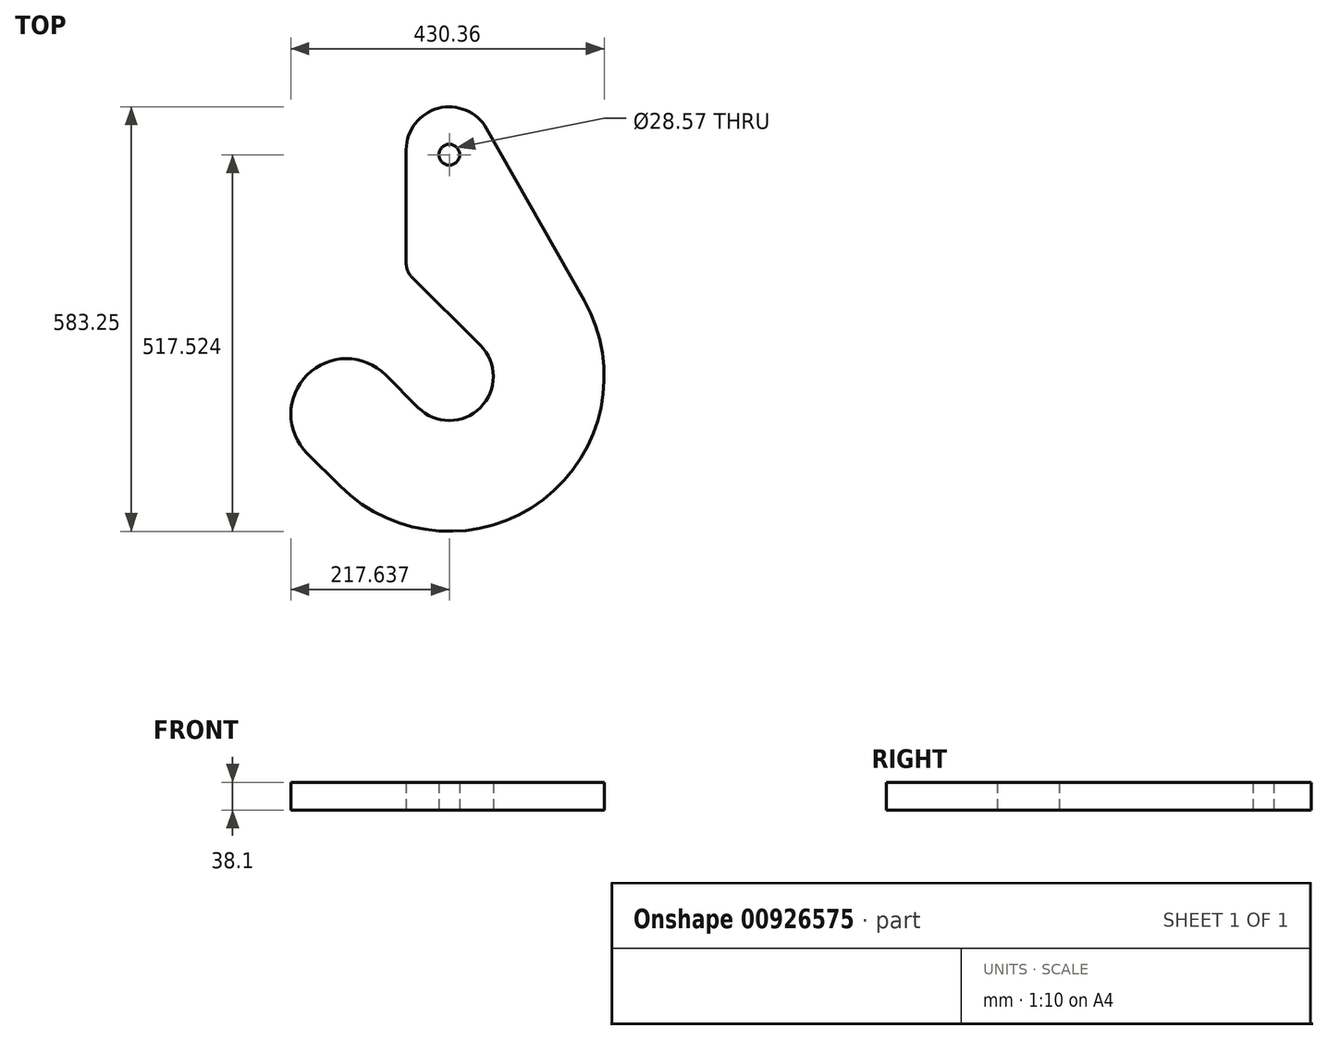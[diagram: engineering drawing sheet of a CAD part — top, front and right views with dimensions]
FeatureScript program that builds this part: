
annotation { "Feature Type Name" : "Feature", "Feature Type Description" : "" }
export const myFeature = defineFeature(function(context is Context, id is Id, definition is map)
    precondition{}
    {
        {
            var Q0;
            Q0=qCreatedBy(makeId("Top.planeOp"),FACE);
            var sketch = newSketch(context, id + "F0", { "sketchPlane" : qUnion([Q0])});
            skCircle(sketch, "E0", {"center": v(-102.2, 33.62) * mm, "radius": 60.33 * mm, "construction": true});
            skLineSegment(sketch, "E1", {"start": v(-102.2, 33.62) * mm, "end": v(-59.55, 76.28) * mm, "construction": true});
            skLineSegment(sketch, "E2", {"start": v(-102.2, 33.62) * mm, "end": v(-144.86, -9.03) * mm, "construction": true});
            skLineSegment(sketch, "E3", {"start": v(-102.2, 33.62) * mm, "end": v(-41.88, 33.62) * mm, "construction": true});
            skLineSegment(sketch, "E4", {"start": v(-102.2, 33.62) * mm, "end": v(-162.53, 33.62) * mm, "construction": true});
            skLineSegment(sketch, "E5", {"start": v(-144.86, -9.03) * mm, "end": v(-189.76, 35.87) * mm});
            skLineSegment(sketch, "E6", {"start": v(-59.55, 76.28) * mm, "end": v(-104.45, 121.18) * mm});
            skLineSegment(sketch, "E7", {"start": v(-189.76, 35.87) * mm, "end": v(-104.45, 121.18) * mm, "construction": true});
            skArc(sketch, "E8", {"start": v(110.52, 33.62) * mm, "mid": v(103.48, 87.92) * mm, "end": v(82.8, 138.62) * mm});
            skArc(sketch, "E9", {"start": v(-252.62, -116.8) * mm, "mid": v(-20.8, -162.9) * mm, "end": v(110.52, 33.62) * mm});
            skLineSegment(sketch, "E10", {"start": v(-144.86, -9.03) * mm, "end": v(-252.62, -116.8) * mm, "construction": true});
            skLineSegment(sketch, "E11", {"start": v(-252.62, -116.8) * mm, "end": v(-297.52, -71.9) * mm});
            skLineSegment(sketch, "E12", {"start": v(-297.52, -71.9) * mm, "end": v(-189.76, 35.87) * mm, "construction": true});
            skArc(sketch, "E13", {"start": v(-297.52, -71.9) * mm, "mid": v(-297.52, 35.87) * mm, "end": v(-189.76, 35.87) * mm});
            skArc(sketch, "E14", {"start": v(-144.86, -9.03) * mm, "mid": v(-59.55, -9.03) * mm, "end": v(-59.55, 76.28) * mm});
            skLineSegment(sketch, "E15", {"start": v(-41.88, 33.62) * mm, "end": v(110.52, 33.62) * mm, "construction": true});
            skLineSegment(sketch, "E16", {"start": v(-104.45, 121.18) * mm, "end": v(-153.93, 170.66) * mm});
            skArc(sketch, "E17", {"start": v(-161.37, 188.62) * mm, "mid": v(-159.43, 178.9) * mm, "end": v(-153.93, 170.66) * mm});
            skLineSegment(sketch, "E18", {"start": v(-102.2, 33.62) * mm, "end": v(-102.2, 404.15) * mm, "construction": true});
            skLineSegment(sketch, "E19", {"start": v(-161.37, 188.62) * mm, "end": v(-161.37, 277.52) * mm});
            skLineSegment(sketch, "E20", {"start": v(-34.37, 345.07) * mm, "end": v(82.8, 138.62) * mm});
            skCircle(sketch, "E21", {"center": v(-102.2, 338.42) * mm, "radius": 14.29 * mm});
            skLineSegment(sketch, "E22", {"start": v(-161.37, 277.52) * mm, "end": v(-161.37, 345.07) * mm});
            skLineSegment(sketch, "E23", {"start": v(-161.37, 345.07) * mm, "end": v(-34.37, 345.07) * mm, "construction": true});
            skLineSegment(sketch, "E24", {"start": v(-34.37, 345.07) * mm, "end": v(-50.92, 374.23) * mm});
            skArc(sketch, "E25", {"start": v(-50.92, 374.23) * mm, "mid": v(-117.37, 402.19) * mm, "end": v(-161.37, 345.07) * mm});
            skPoint(sketch, "E26", {"position": v(-102.2, 352.71) * mm});
            skSolve(sketch);
        }
        {
            var Q0;
            Q0=makeQuery(id+"F0.imprint","IMPRINT",FACE,{"disambiguationData":[TD([[makeQuery(id+"F0.imprint","IMPRINT",EDGE,{"derivedFrom":sQuery(id+"F0.wireOp",EDGE,"E5")}),1.0]])]});
            extrude(context, id + "F1", {"entities" : qUnion([Q0]), "depth" : 38.1 * mm, "offsetDistance" : 25.4 * mm});
        }
    });
